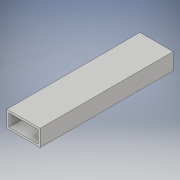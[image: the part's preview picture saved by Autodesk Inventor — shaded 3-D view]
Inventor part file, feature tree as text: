
AUTODESK INVENTOR PART (.ipt)
format: ipt  version: 2019 (Build 230136000, 136)  size: 95,744 bytes
history: native  units: in
note: dims shown in document units (in); Inventor stores cm internally (conversion verified against a paired STEP export)
features: extrude x1, sketch x1
ambient origin geometry x8: Origin, YZ Plane, XZ Plane, XY Plane, X Axis, Y Axis, Z Axis, Center Point
bodies: Solid1 (feature_tree)
feature tree (2):
  extrude  "Extrusion1"  Depth=1.0in
  sketch  "Sketch1"  dims[d0=2.0in d1=1.0in d2=0.125in d3=8.0in d4=0.0in]
